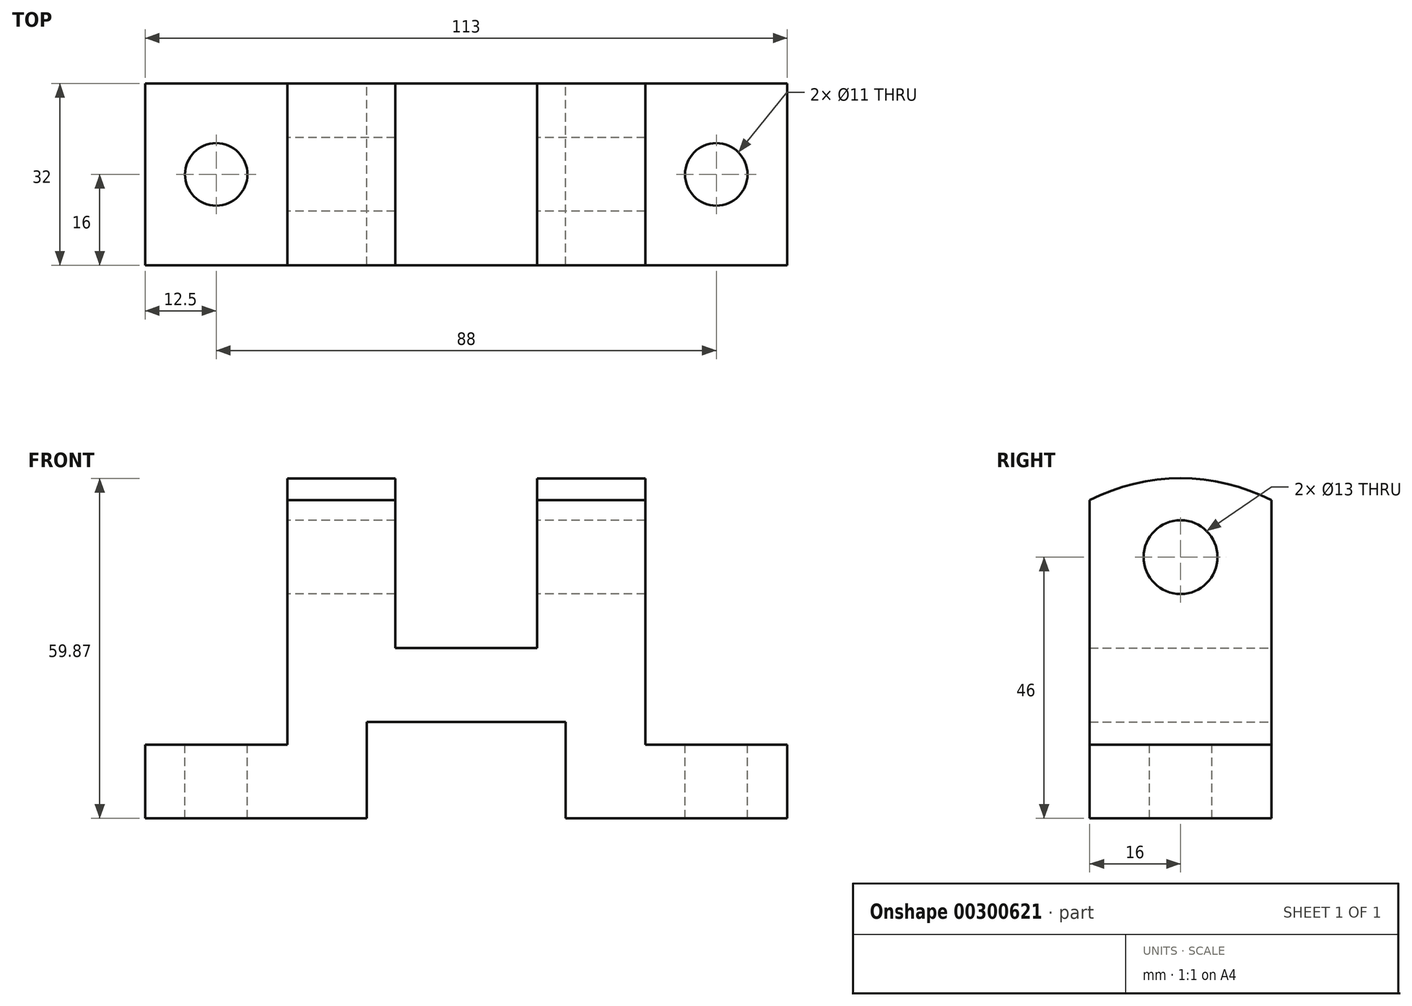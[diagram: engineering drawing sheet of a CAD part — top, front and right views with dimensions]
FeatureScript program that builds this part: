
annotation { "Feature Type Name" : "Feature", "Feature Type Description" : "" }
export const myFeature = defineFeature(function(context is Context, id is Id, definition is map)
    precondition{}
    {
        {
            var Q0;
            Q0=qCreatedBy(makeId("Front.planeOp"),FACE);
            var sketch = newSketch(context, id + "F0", { "sketchPlane" : qUnion([Q0])});
            skLineSegment(sketch, "E0", {"start": v(56.5, 0) * mm, "end": v(56.5, 13) * mm});
            skLineSegment(sketch, "E1", {"start": v(56.5, 13) * mm, "end": v(31.5, 13) * mm});
            skLineSegment(sketch, "E2", {"start": v(31.5, 13) * mm, "end": v(31.5, 64) * mm});
            skLineSegment(sketch, "E3", {"start": v(31.5, 64) * mm, "end": v(12.5, 64) * mm});
            skLineSegment(sketch, "E4", {"start": v(12.5, 64) * mm, "end": v(12.5, 30) * mm});
            skLineSegment(sketch, "E5", {"start": v(12.5, 30) * mm, "end": v(-12.5, 30) * mm});
            skLineSegment(sketch, "E6", {"start": v(-12.5, 30) * mm, "end": v(-12.5, 64) * mm});
            skLineSegment(sketch, "E7", {"start": v(-12.5, 64) * mm, "end": v(-31.5, 64) * mm});
            skLineSegment(sketch, "E8", {"start": v(-31.5, 64) * mm, "end": v(-31.5, 13) * mm});
            skLineSegment(sketch, "E9", {"start": v(-31.5, 13) * mm, "end": v(-56.5, 13) * mm});
            skLineSegment(sketch, "E10", {"start": v(-56.5, 13) * mm, "end": v(-56.5, 0) * mm});
            skLineSegment(sketch, "E11", {"start": v(-17.5, 0) * mm, "end": v(-17.5, 17) * mm});
            skLineSegment(sketch, "E12", {"start": v(-17.5, 17) * mm, "end": v(17.5, 17) * mm});
            skLineSegment(sketch, "E13", {"start": v(17.5, 17) * mm, "end": v(17.5, 0) * mm});
            skLineSegment(sketch, "E14", {"start": v(-17.5, 0) * mm, "end": v(-56.5, 0) * mm});
            skLineSegment(sketch, "E15", {"start": v(17.5, 0) * mm, "end": v(56.5, 0) * mm});
            skSolve(sketch);
        }
        {
            var Q0;
            Q0=makeQuery(id+"F0.imprint","IMPRINT",FACE,{"disambiguationData":[TD([[makeQuery(id+"F0.imprint","IMPRINT",EDGE,{"derivedFrom":sQuery(id+"F0.wireOp",EDGE,"E0")}),1.0]])]});
            extrude(context, id + "F1", {"entities" : qUnion([Q0]), "depth" : 32 * mm});
        }
        {
            var Q0;
            Q0=makeQuery(id+"F1.opExtrude","SWEPT_FACE",FACE,{"disambiguationData":[OSD([sQuery(id+"F0.wireOp",EDGE,"E9")])]});
            var sketch = newSketch(context, id + "F2", { "sketchPlane" : qUnion([Q0])});
            skCircle(sketch, "E16", {"center": v(-44, -16) * mm, "radius": 5.5 * mm});
            skPoint(sketch, "E16.centerSnap0", {"position": v(-56.5, -16) * mm});
            skPoint(sketch, "E16.centerSnap1", {"position": v(-44, 0) * mm});
            skSolve(sketch);
        }
        {
            var Q0;
            Q0=makeQuery(id+"F1.opExtrude","SWEPT_FACE",FACE,{"disambiguationData":[OSD([sQuery(id+"F0.wireOp",EDGE,"E1")])]});
            var sketch = newSketch(context, id + "F3", { "sketchPlane" : qUnion([Q0])});
            skCircle(sketch, "E17", {"center": v(44, -16) * mm, "radius": 5.5 * mm});
            skPoint(sketch, "E17.centerSnap0", {"position": v(56.5, -16) * mm});
            skPoint(sketch, "E17.centerSnap1", {"position": v(44, 0) * mm});
            skSolve(sketch);
        }
        {
            var Q0;
            Q0=makeQuery(id+"F2.imprint","IMPRINT",FACE,{"disambiguationData":[TD([[makeQuery(id+"F2.imprint","IMPRINT",EDGE,{"derivedFrom":sQuery(id+"F2.wireOp",EDGE,"E16")}),1.0]])]});
            extrude(context, id + "F4", {"entities" : qUnion([Q0]), "operationType" : NewBodyOperationType.REMOVE, "endBound" : BoundingType.THROUGH_ALL, "oppositeDirection" : true, "depth" : 25 * mm});
        }
        {
            var Q0;
            Q0=makeQuery(id+"F3.imprint","IMPRINT",FACE,{"disambiguationData":[TD([[makeQuery(id+"F3.imprint","IMPRINT",EDGE,{"derivedFrom":sQuery(id+"F3.wireOp",EDGE,"E17")}),1.0]])]});
            extrude(context, id + "F5", {"entities" : qUnion([Q0]), "operationType" : NewBodyOperationType.REMOVE, "endBound" : BoundingType.THROUGH_ALL, "oppositeDirection" : true, "depth" : 25 * mm});
        }
        {
            var Q0;
            Q0=makeQuery(id+"F1.opExtrude","SWEPT_FACE",FACE,{"disambiguationData":[OSD([sQuery(id+"F0.wireOp",EDGE,"E8")])]});
            var sketch = newSketch(context, id + "F6", { "sketchPlane" : qUnion([Q0])});
            skPoint(sketch, "E18.startSnap0", {"position": v(16, 13) * mm});
            skLineSegment(sketch, "E19", {"start": v(16, 0) * mm, "end": v(16, 46) * mm});
            skCircle(sketch, "E20", {"center": v(16, 46) * mm, "radius": 6.5 * mm});
            skSolve(sketch);
        }
        {
            var Q0;
            Q0=makeQuery(id+"F6.imprint","IMPRINT",FACE,{"disambiguationData":[TD([[makeQuery(id+"F6.imprint","IMPRINT",EDGE,{"derivedFrom":sQuery(id+"F6.wireOp",EDGE,"E20")}),1.0]])]});
            extrude(context, id + "F7", {"entities" : qUnion([Q0]), "operationType" : NewBodyOperationType.REMOVE, "endBound" : BoundingType.THROUGH_ALL, "oppositeDirection" : true, "depth" : 25 * mm});
        }
        {
            var Q0;
            Q0=makeQuery(id+"F1.opExtrude","SWEPT_FACE",FACE,{"disambiguationData":[OSD([sQuery(id+"F0.wireOp",EDGE,"E8")])]});
            var sketch = newSketch(context, id + "F8", { "sketchPlane" : qUnion([Q0])});
            skArc(sketch, "E21", {"start": v(32, 56) * mm, "mid": v(16, 59.87) * mm, "end": v(0, 56) * mm});
            skSolve(sketch);
        }
        {
            var Q0;
            {var subQ0=sQuery(id+"F8.wireOp",EDGE,"E21");Q0=makeQuery(id+"F8.imprint","IMPRINT",FACE,{"disambiguationData":[TD([[makeQuery(id+"F8.imprint","IMPRINT",EDGE,{"derivedFrom":subQ0}),-1.0]])]});}
            extrude(context, id + "F9", {"entities" : qUnion([Q0]), "operationType" : NewBodyOperationType.REMOVE, "endBound" : BoundingType.THROUGH_ALL, "oppositeDirection" : true, "depth" : 25 * mm});
        }
    });
